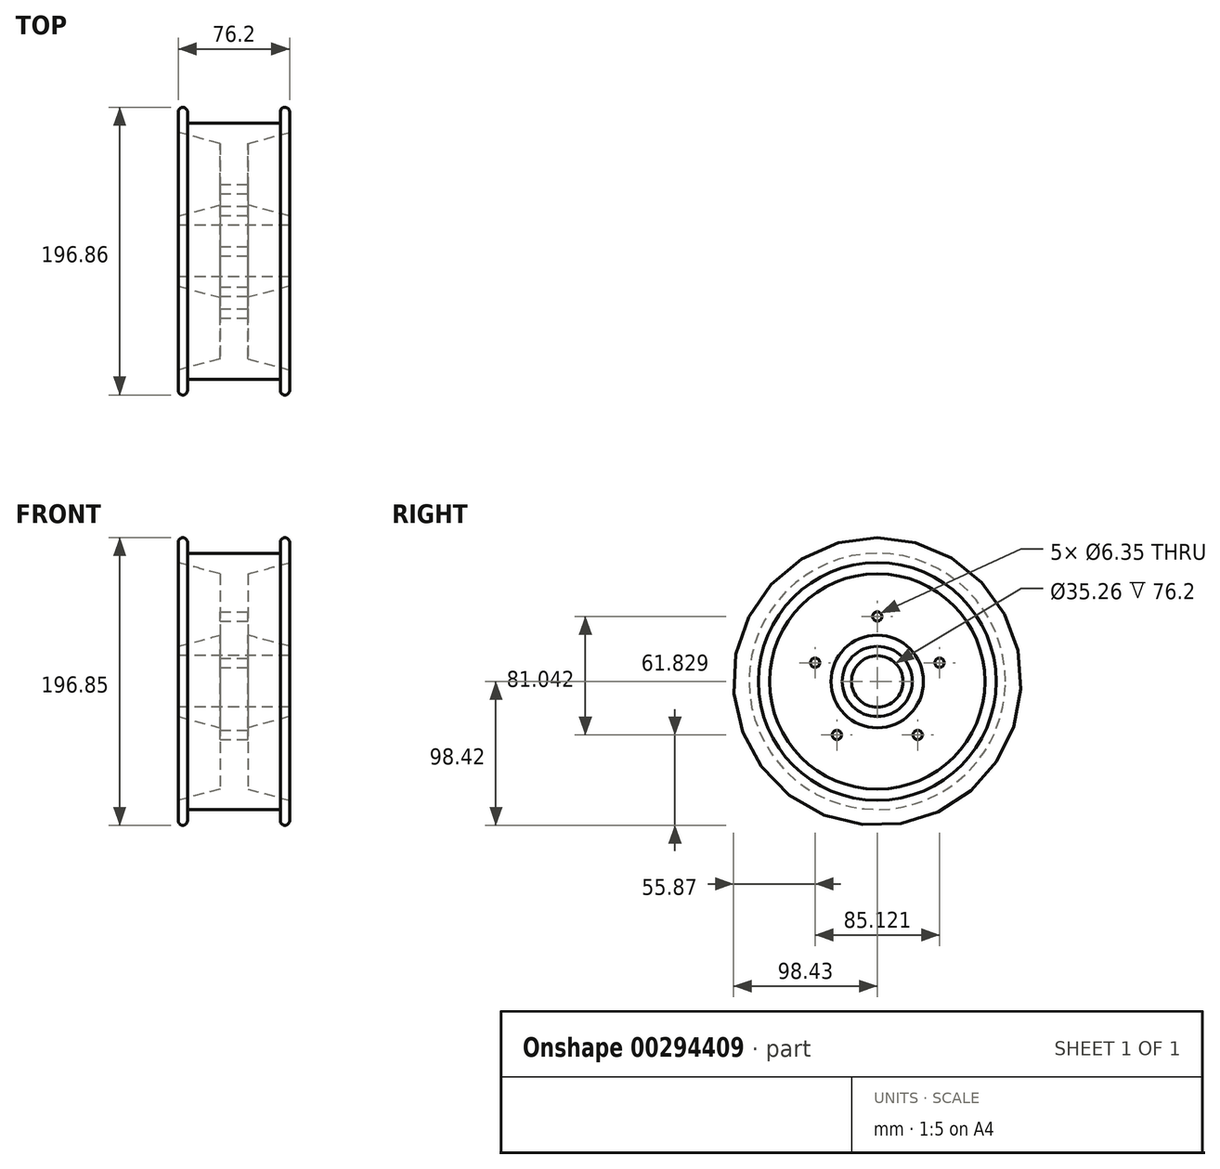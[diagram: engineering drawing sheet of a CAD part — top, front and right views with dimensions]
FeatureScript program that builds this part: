
annotation { "Feature Type Name" : "Feature", "Feature Type Description" : "" }
export const myFeature = defineFeature(function(context is Context, id is Id, definition is map)
    precondition{}
    {
        {
            var Q0;
            Q0=qCreatedBy(makeId("Front.planeOp"),FACE);
            var sketch = newSketch(context, id + "F0", { "sketchPlane" : qUnion([Q0])});
            skPoint(sketch, "E0", {"position": v(0, -42.85) * mm});
            skPoint(sketch, "E1", {"position": v(88.32, -42.85) * mm});
            skLineSegment(sketch, "E2", {"start": v(9.52, 30.77) * mm, "end": v(9.53, -11.22) * mm});
            skLineSegment(sketch, "E3", {"start": v(9.52, -11.22) * mm, "end": v(38.1, -18.87) * mm});
            skLineSegment(sketch, "E4", {"start": v(38.1, -18.87) * mm, "end": v(38.1, -25.22) * mm});
            skLineSegment(sketch, "E5", {"start": v(38.1, -25.22) * mm, "end": v(0, -25.22) * mm});
            skLineSegment(sketch, "E6", {"start": v(9.52, 30.77) * mm, "end": v(38.1, 38.43) * mm});
            skLineSegment(sketch, "E7", {"start": v(31.75, 44.78) * mm, "end": v(31.75, 52.4) * mm});
            skLineSegment(sketch, "E8", {"start": v(38.1, 38.43) * mm, "end": v(38.1, 52.4) * mm});
            skLineSegment(sketch, "E9.MirrorCS", {"start": v(-9.52, 30.77) * mm, "end": v(-38.1, 38.43) * mm});
            skLineSegment(sketch, "E10.MirrorCS", {"start": v(-38.1, 38.43) * mm, "end": v(-38.1, 52.4) * mm});
            skLineSegment(sketch, "E11.MirrorCS", {"start": v(-9.52, 30.77) * mm, "end": v(-9.52, -11.22) * mm});
            skLineSegment(sketch, "E12.MirrorCS", {"start": v(-38.1, -25.22) * mm, "end": v(0, -25.22) * mm});
            skLineSegment(sketch, "E13.MirrorCS", {"start": v(-9.52, -11.22) * mm, "end": v(-38.1, -18.87) * mm});
            skLineSegment(sketch, "E14.MirrorCS", {"start": v(-38.1, -18.87) * mm, "end": v(-38.1, -25.22) * mm});
            skLineSegment(sketch, "E15.MirrorCS", {"start": v(-31.75, 44.78) * mm, "end": v(-31.75, 52.4) * mm});
            skArc(sketch, "E16", {"start": v(31.75, 52.4) * mm, "mid": v(34.93, 55.58) * mm, "end": v(38.1, 52.4) * mm});
            skArc(sketch, "E17.MirrorCS", {"start": v(-31.75, 52.4) * mm, "mid": v(-34.93, 55.58) * mm, "end": v(-38.1, 52.4) * mm});
            skLineSegment(sketch, "E18", {"start": v(-31.75, 44.78) * mm, "end": v(31.75, 44.78) * mm});
            skLineSegment(sketch, "E19", {"start": v(0, -42.85) * mm, "end": v(88.32, -42.85) * mm});
            skSolve(sketch);
        }
        {
            var Q0;
            Q0 = qSketchRegion(id + "F0", true);
            var Q1;
            Q1=sQuery(id+"F0.wireOp",EDGE,"E19");
            revolve(context, id + "F1", {"entities" : qUnion([Q0]), "axis" : qUnion([Q1]), "revolveType" : RevolveType.FULL});
        }
        {
            var Q0;
            Q0=makeQuery(id+"F1.opRevolve","SWEPT_FACE",FACE,{"disambiguationData":[OSD([sQuery(id+"F0.wireOp",EDGE,"E2")])]});
            var sketch = newSketch(context, id + "F2", { "sketchPlane" : qUnion([Q0])});
            skCircle(sketch, "E20", {"center": v(0, 1.6) * mm, "radius": 3.81 * mm});
            skCircle(sketch, "E21", {"center": v(42.56, -30.03) * mm, "radius": 3.81 * mm});
            skCircle(sketch, "E22", {"center": v(27.64, -79.44) * mm, "radius": 3.81 * mm});
            skCircle(sketch, "E23.MirrorC", {"center": v(-42.56, -30.03) * mm, "radius": 3.81 * mm});
            skCircle(sketch, "E24.MirrorC", {"center": v(-27.64, -79.44) * mm, "radius": 3.81 * mm});
            skCircle(sketch, "E25", {"center": v(0, -42.85) * mm, "radius": 44.45 * mm});
            skSolve(sketch);
        }
        {
            var Q0;
            Q0=sQuery(id+"F2.wireOp",VERTEX,"E23.MirrorC.center");
            var Q1;
            Q1=makeQuery(id+"F1.opRevolve","SWEPT_BODY",BODY,{"disambiguationData":[OSD([sQuery(id+"F0.wireOp",EDGE,"E2"),sQuery(id+"F0.wireOp",EDGE,"E3"),sQuery(id+"F0.wireOp",EDGE,"E4"),sQuery(id+"F0.wireOp",EDGE,"E5"),sQuery(id+"F0.wireOp",EDGE,"E6"),sQuery(id+"F0.wireOp",EDGE,"E7"),sQuery(id+"F0.wireOp",EDGE,"E8"),sQuery(id+"F0.wireOp",EDGE,"E9.MirrorCS"),sQuery(id+"F0.wireOp",EDGE,"E10.MirrorCS"),sQuery(id+"F0.wireOp",EDGE,"E11.MirrorCS"),sQuery(id+"F0.wireOp",EDGE,"E12.MirrorCS"),sQuery(id+"F0.wireOp",EDGE,"E13.MirrorCS"),sQuery(id+"F0.wireOp",EDGE,"E14.MirrorCS"),sQuery(id+"F0.wireOp",EDGE,"E15.MirrorCS"),sQuery(id+"F0.wireOp",EDGE,"E16"),sQuery(id+"F0.wireOp",EDGE,"E17.MirrorCS"),sQuery(id+"F0.wireOp",EDGE,"E18")])]});
            hole(context, id + "F3", {"style" : HoleStyle.SIMPLE, "endStyle" : HoleEndStyle.THROUGH, "holeDiameter" : 6.35 * mm, "tappedDepth" : 12.7 * mm, "tapClearance" : 3, "locations" : qUnion([Q0]), "scope" : qUnion([Q1])});
        }
        {
            var Q0;
            Q0=sQuery(id+"F2.wireOp",VERTEX,"E20.center");
            var Q1;
            Q1=makeQuery(id+"F1.opRevolve","SWEPT_BODY",BODY,{"disambiguationData":[OSD([sQuery(id+"F0.wireOp",EDGE,"E2"),sQuery(id+"F0.wireOp",EDGE,"E3"),sQuery(id+"F0.wireOp",EDGE,"E4"),sQuery(id+"F0.wireOp",EDGE,"E5"),sQuery(id+"F0.wireOp",EDGE,"E6"),sQuery(id+"F0.wireOp",EDGE,"E7"),sQuery(id+"F0.wireOp",EDGE,"E8"),sQuery(id+"F0.wireOp",EDGE,"E9.MirrorCS"),sQuery(id+"F0.wireOp",EDGE,"E10.MirrorCS"),sQuery(id+"F0.wireOp",EDGE,"E11.MirrorCS"),sQuery(id+"F0.wireOp",EDGE,"E12.MirrorCS"),sQuery(id+"F0.wireOp",EDGE,"E13.MirrorCS"),sQuery(id+"F0.wireOp",EDGE,"E14.MirrorCS"),sQuery(id+"F0.wireOp",EDGE,"E15.MirrorCS"),sQuery(id+"F0.wireOp",EDGE,"E16"),sQuery(id+"F0.wireOp",EDGE,"E17.MirrorCS"),sQuery(id+"F0.wireOp",EDGE,"E18")])]});
            hole(context, id + "F4", {"style" : HoleStyle.SIMPLE, "endStyle" : HoleEndStyle.THROUGH, "holeDiameter" : 6.35 * mm, "tappedDepth" : 12.7 * mm, "tapClearance" : 3, "locations" : qUnion([Q0]), "scope" : qUnion([Q1])});
        }
        {
            var Q0;
            Q0=sQuery(id+"F2.wireOp",VERTEX,"E24.MirrorC.center");
            var Q1;
            Q1=makeQuery(id+"F1.opRevolve","SWEPT_BODY",BODY,{"disambiguationData":[OSD([sQuery(id+"F0.wireOp",EDGE,"E2"),sQuery(id+"F0.wireOp",EDGE,"E3"),sQuery(id+"F0.wireOp",EDGE,"E4"),sQuery(id+"F0.wireOp",EDGE,"E5"),sQuery(id+"F0.wireOp",EDGE,"E6"),sQuery(id+"F0.wireOp",EDGE,"E7"),sQuery(id+"F0.wireOp",EDGE,"E8"),sQuery(id+"F0.wireOp",EDGE,"E9.MirrorCS"),sQuery(id+"F0.wireOp",EDGE,"E10.MirrorCS"),sQuery(id+"F0.wireOp",EDGE,"E11.MirrorCS"),sQuery(id+"F0.wireOp",EDGE,"E12.MirrorCS"),sQuery(id+"F0.wireOp",EDGE,"E13.MirrorCS"),sQuery(id+"F0.wireOp",EDGE,"E14.MirrorCS"),sQuery(id+"F0.wireOp",EDGE,"E15.MirrorCS"),sQuery(id+"F0.wireOp",EDGE,"E16"),sQuery(id+"F0.wireOp",EDGE,"E17.MirrorCS"),sQuery(id+"F0.wireOp",EDGE,"E18")])]});
            hole(context, id + "F5", {"style" : HoleStyle.SIMPLE, "endStyle" : HoleEndStyle.THROUGH, "holeDiameter" : 6.35 * mm, "tappedDepth" : 12.7 * mm, "tapClearance" : 3, "locations" : qUnion([Q0]), "scope" : qUnion([Q1])});
        }
        {
            var Q0;
            Q0=sQuery(id+"F2.wireOp",VERTEX,"E22.center");
            var Q1;
            Q1=makeQuery(id+"F1.opRevolve","SWEPT_BODY",BODY,{"disambiguationData":[OSD([sQuery(id+"F0.wireOp",EDGE,"E2"),sQuery(id+"F0.wireOp",EDGE,"E3"),sQuery(id+"F0.wireOp",EDGE,"E4"),sQuery(id+"F0.wireOp",EDGE,"E5"),sQuery(id+"F0.wireOp",EDGE,"E6"),sQuery(id+"F0.wireOp",EDGE,"E7"),sQuery(id+"F0.wireOp",EDGE,"E8"),sQuery(id+"F0.wireOp",EDGE,"E9.MirrorCS"),sQuery(id+"F0.wireOp",EDGE,"E10.MirrorCS"),sQuery(id+"F0.wireOp",EDGE,"E11.MirrorCS"),sQuery(id+"F0.wireOp",EDGE,"E12.MirrorCS"),sQuery(id+"F0.wireOp",EDGE,"E13.MirrorCS"),sQuery(id+"F0.wireOp",EDGE,"E14.MirrorCS"),sQuery(id+"F0.wireOp",EDGE,"E15.MirrorCS"),sQuery(id+"F0.wireOp",EDGE,"E16"),sQuery(id+"F0.wireOp",EDGE,"E17.MirrorCS"),sQuery(id+"F0.wireOp",EDGE,"E18")])]});
            hole(context, id + "F6", {"style" : HoleStyle.SIMPLE, "endStyle" : HoleEndStyle.THROUGH, "holeDiameter" : 6.35 * mm, "tappedDepth" : 12.7 * mm, "tapClearance" : 3, "locations" : qUnion([Q0]), "scope" : qUnion([Q1])});
        }
        {
            var Q0;
            Q0=sQuery(id+"F2.wireOp",VERTEX,"E21.center");
            var Q1;
            Q1=makeQuery(id+"F1.opRevolve","SWEPT_BODY",BODY,{"disambiguationData":[OSD([sQuery(id+"F0.wireOp",EDGE,"E2"),sQuery(id+"F0.wireOp",EDGE,"E3"),sQuery(id+"F0.wireOp",EDGE,"E4"),sQuery(id+"F0.wireOp",EDGE,"E5"),sQuery(id+"F0.wireOp",EDGE,"E6"),sQuery(id+"F0.wireOp",EDGE,"E7"),sQuery(id+"F0.wireOp",EDGE,"E8"),sQuery(id+"F0.wireOp",EDGE,"E9.MirrorCS"),sQuery(id+"F0.wireOp",EDGE,"E10.MirrorCS"),sQuery(id+"F0.wireOp",EDGE,"E11.MirrorCS"),sQuery(id+"F0.wireOp",EDGE,"E12.MirrorCS"),sQuery(id+"F0.wireOp",EDGE,"E13.MirrorCS"),sQuery(id+"F0.wireOp",EDGE,"E14.MirrorCS"),sQuery(id+"F0.wireOp",EDGE,"E15.MirrorCS"),sQuery(id+"F0.wireOp",EDGE,"E16"),sQuery(id+"F0.wireOp",EDGE,"E17.MirrorCS"),sQuery(id+"F0.wireOp",EDGE,"E18")])]});
            hole(context, id + "F7", {"style" : HoleStyle.SIMPLE, "endStyle" : HoleEndStyle.THROUGH, "holeDiameter" : 6.35 * mm, "tappedDepth" : 12.7 * mm, "tapClearance" : 3, "locations" : qUnion([Q0]), "scope" : qUnion([Q1])});
        }
    });
